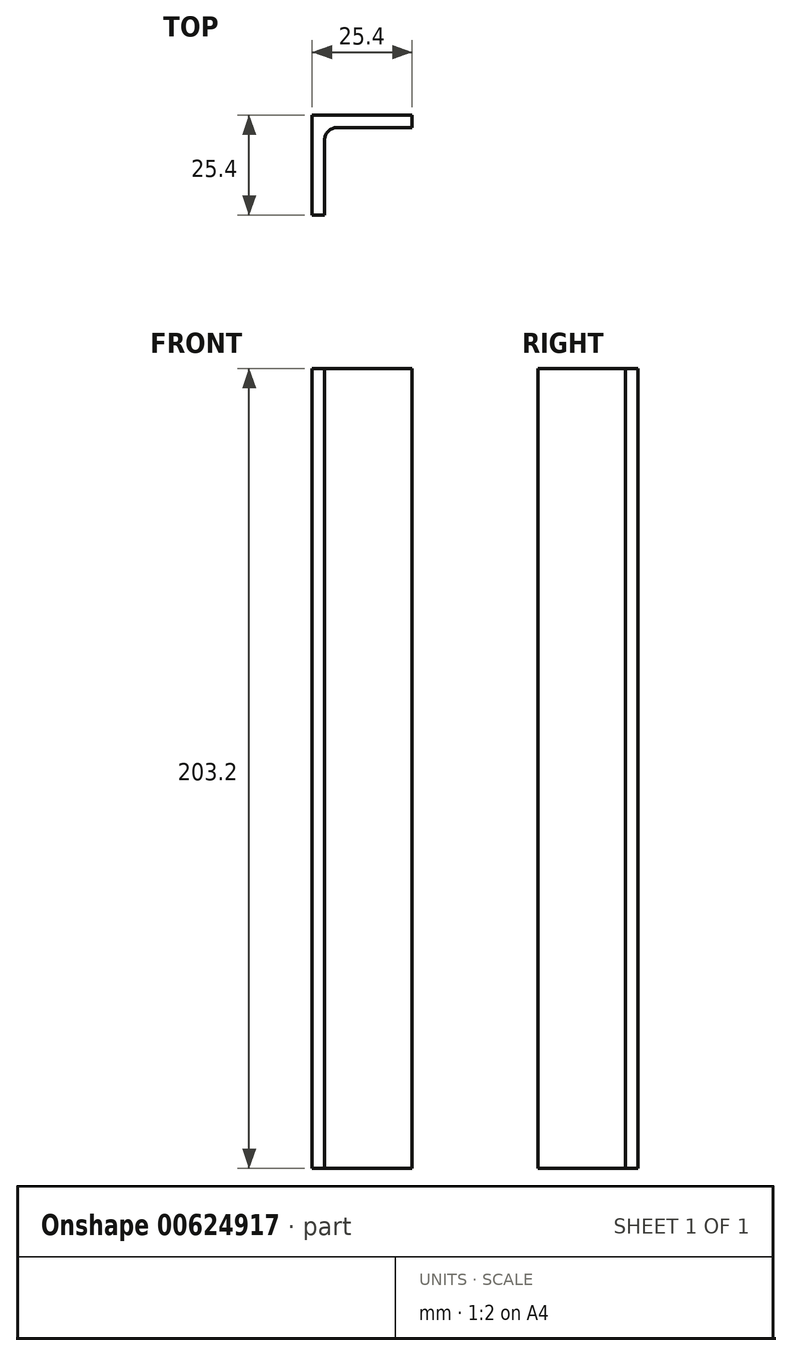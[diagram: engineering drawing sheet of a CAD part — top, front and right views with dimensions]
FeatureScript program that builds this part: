
annotation { "Feature Type Name" : "Feature", "Feature Type Description" : "" }
export const myFeature = defineFeature(function(context is Context, id is Id, definition is map)
    precondition{}
    {
        {
            var Q0;
            Q0=qCreatedBy(makeId("Top.planeOp"),FACE);
            var sketch = newSketch(context, id + "F0", { "sketchPlane" : qUnion([Q0])});
            skLineSegment(sketch, "E0", {"start": v(0, 0) * mm, "end": v(0, -25.4) * mm});
            skLineSegment(sketch, "E1", {"start": v(0, -25.4) * mm, "end": v(3.18, -25.4) * mm});
            skLineSegment(sketch, "E2", {"start": v(3.18, -25.4) * mm, "end": v(3.18, -3.18) * mm});
            skLineSegment(sketch, "E3", {"start": v(3.18, -3.18) * mm, "end": v(25.4, -3.18) * mm});
            skLineSegment(sketch, "E4", {"start": v(25.4, -3.18) * mm, "end": v(25.4, 0) * mm});
            skLineSegment(sketch, "E5", {"start": v(25.4, 0) * mm, "end": v(0, 0) * mm});
            skSolve(sketch);
        }
        {
            var Q0;
            Q0=makeQuery(id+"F0.imprint","IMPRINT",FACE,{"disambiguationData":[TD([[makeQuery(id+"F0.imprint","IMPRINT",EDGE,{"derivedFrom":sQuery(id+"F0.wireOp",EDGE,"E0")}),1.0]])]});
            extrude(context, id + "F1", {"entities" : qUnion([Q0]), "depth" : 203.2 * mm, "offsetDistance" : 25.4 * mm});
        }
        {
            var Q0;
            Q0=makeQuery(id+"F1.opExtrude","SWEPT_EDGE",EDGE,{"disambiguationData":[OSD([sQuery(id+"F0.wireOp",EDGE,"E2"),sQuery(id+"F0.wireOp",EDGE,"E3")])]});
            fillet(context, id + "F2", {"entities" : qUnion([Q0]), "radius" : 3.17 * mm, "tangentPropagation" : true, "allowEdgeOverflow" : false});
        }
    });
